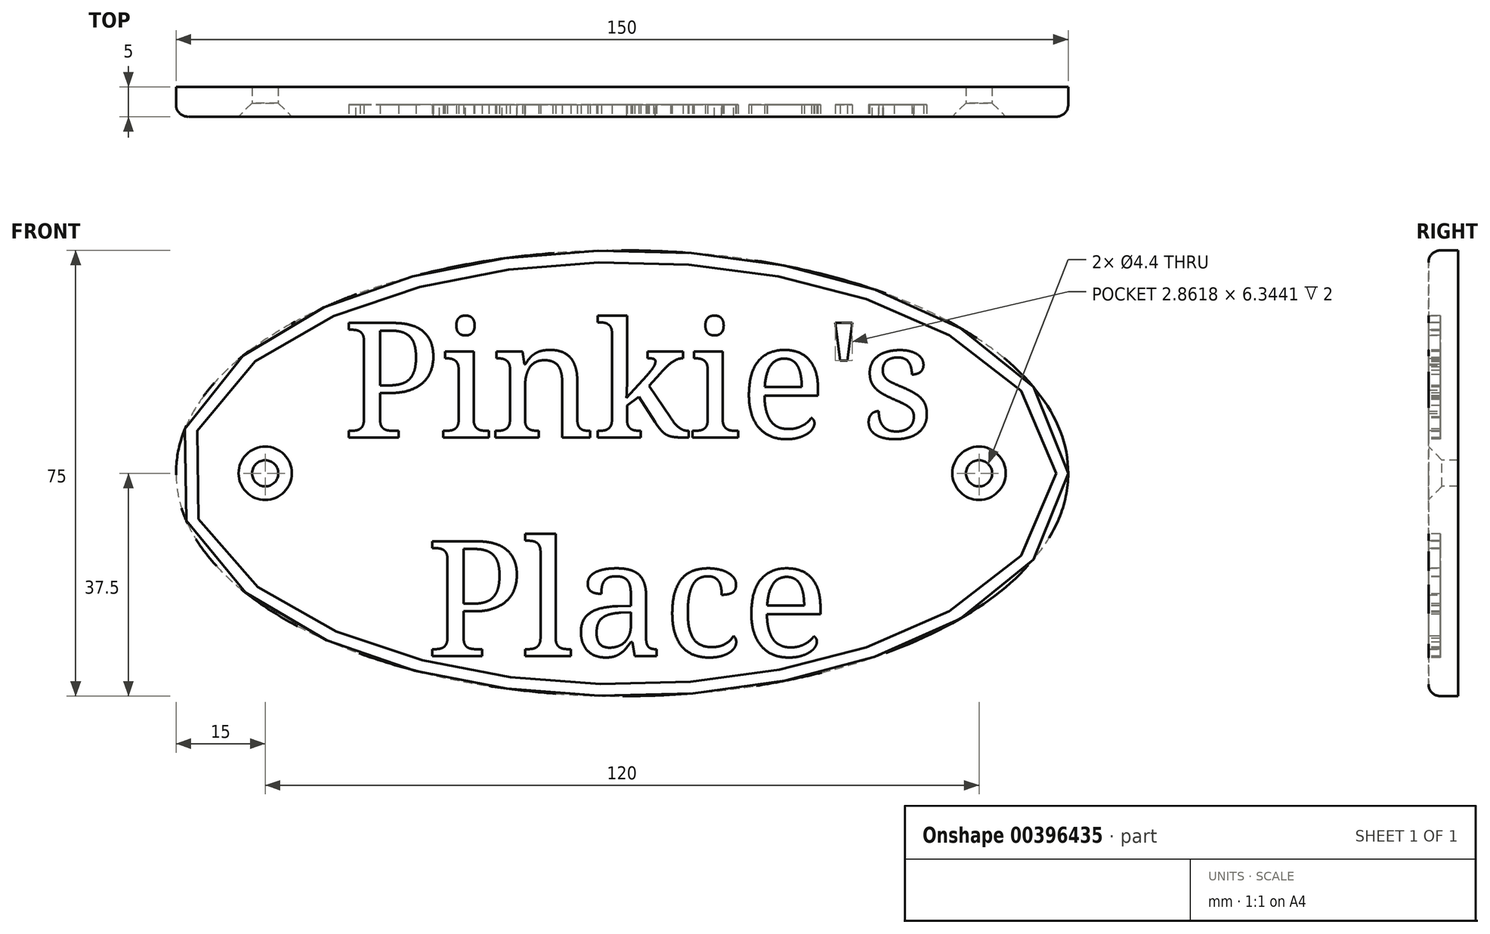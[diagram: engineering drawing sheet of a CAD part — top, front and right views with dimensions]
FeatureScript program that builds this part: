
annotation { "Feature Type Name" : "Feature", "Feature Type Description" : "" }
export const myFeature = defineFeature(function(context is Context, id is Id, definition is map)
    precondition{}
    {
        {
            var Q0;
            Q0=qCreatedBy(makeId("Front.planeOp"),FACE);
            var sketch = newSketch(context, id + "F0", { "sketchPlane" : qUnion([Q0])});
            skEllipse(sketch, "E0", {"center": v(0, 0) * mm, "majorRadius": 75 * mm, "minorRadius": 37.5 * mm, "majorAxis": v(1, 0)});
            skSolve(sketch);
        }
        {
            var Q0;
            Q0 = qSketchRegion(id + "F0", true);
            extrude(context, id + "F1", {"entities" : qUnion([Q0]), "oppositeDirection" : true, "depth" : 5 * mm});
        }
        {
            var Q0;
            Q0=makeQuery(id+"F1.opExtrude","CAP_FACE",FACE,{"disambiguationData":[OSD([sQuery(id+"F0.wireOp",EDGE,"E0")])],"isStart":true});
            var sketch = newSketch(context, id + "F2", { "sketchPlane" : qUnion([Q0])});
            skText(sketch, "E1", { "text": "Pinkie\'s\n  Place", "fontName": "NotoSerif-Regular.ttf"});
            const initialGuessF2  = {"E1": [-0.047, 0.006, 1, 0, 0.01945]};
            skSetInitialGuess(sketch, initialGuessF2);
            skSolve(sketch);
        }
        {
            var Q0;
            Q0 = qSketchRegion(id + "F2", true);
            extrude(context, id + "F3", {"entities" : qUnion([Q0]), "operationType" : NewBodyOperationType.REMOVE, "oppositeDirection" : true, "depth" : 2 * mm});
        }
        {
            var Q0;
            {var subQ0=sQuery(id+"F0.wireOp",EDGE,"E0");Q0=makeQuery(id+"F3.boolean.opBoolean","SPLIT",FACE,{"disambiguationData":[TD([makeQuery(id+"F1.opExtrude","SWEPT_FACE",FACE,{"disambiguationData":[OSD([subQ0])]})])],"derivedFrom":makeQuery(id+"F1.opExtrude","CAP_FACE",FACE,{"disambiguationData":[OSD([subQ0])],"isStart":true})});}
            var sketch = newSketch(context, id + "F4", { "sketchPlane" : qUnion([Q0])});
            skPoint(sketch, "E2", {"position": v(0, 0) * mm});
            skPoint(sketch, "E3", {"position": v(-60, 0) * mm});
            skPoint(sketch, "E4.MirrorP", {"position": v(60, 0) * mm});
            skSolve(sketch);
        }
        {
            var Q0;
            Q0=sQuery(id+"F4.wireOp",VERTEX,"E3");
            var Q1;
            Q1=sQuery(id+"F4.wireOp",VERTEX,"E4.MirrorP");
            var Q2;
            Q2=makeQuery(id+"F1.opExtrude","SWEPT_BODY",BODY,{"disambiguationData":[OSD([sQuery(id+"F0.wireOp",EDGE,"E0")])]});
            hole(context, id + "F5", {"style" : HoleStyle.C_SINK, "endStyle" : HoleEndStyle.THROUGH, "standardTappedOrClearance" : lookupTablePath({ "standard" : "ISO", "fit" : "Normal", "size" : "M4", "type" : "Clearance" }), "standardBlindInLast" : lookupTablePath({ "fit" : "Standard", "standard" : "ISO", "size" : "M4", "type" : "Clearance" }), "holeDiameter" : 4.4 * mm, "cSinkDiameter" : 8.96 * mm, "cSinkAngle" : 90 * degree, "isTappedThrough" : true, "tappedDepth" : 12 * mm, "tapClearance" : 3, "locations" : qUnion([Q0, Q1]), "scope" : qUnion([Q2])});
        }
        {
            var Q0;
            Q0=makeQuery(id+"F1.opExtrude","CAP_EDGE",EDGE,{"disambiguationData":[OSD([sQuery(id+"F0.wireOp",EDGE,"E0")])],"isStart":true});
            fillet(context, id + "F6", {"entities" : qUnion([Q0]), "radius" : 2 * mm, "tangentPropagation" : true, "allowEdgeOverflow" : false});
        }
    });
